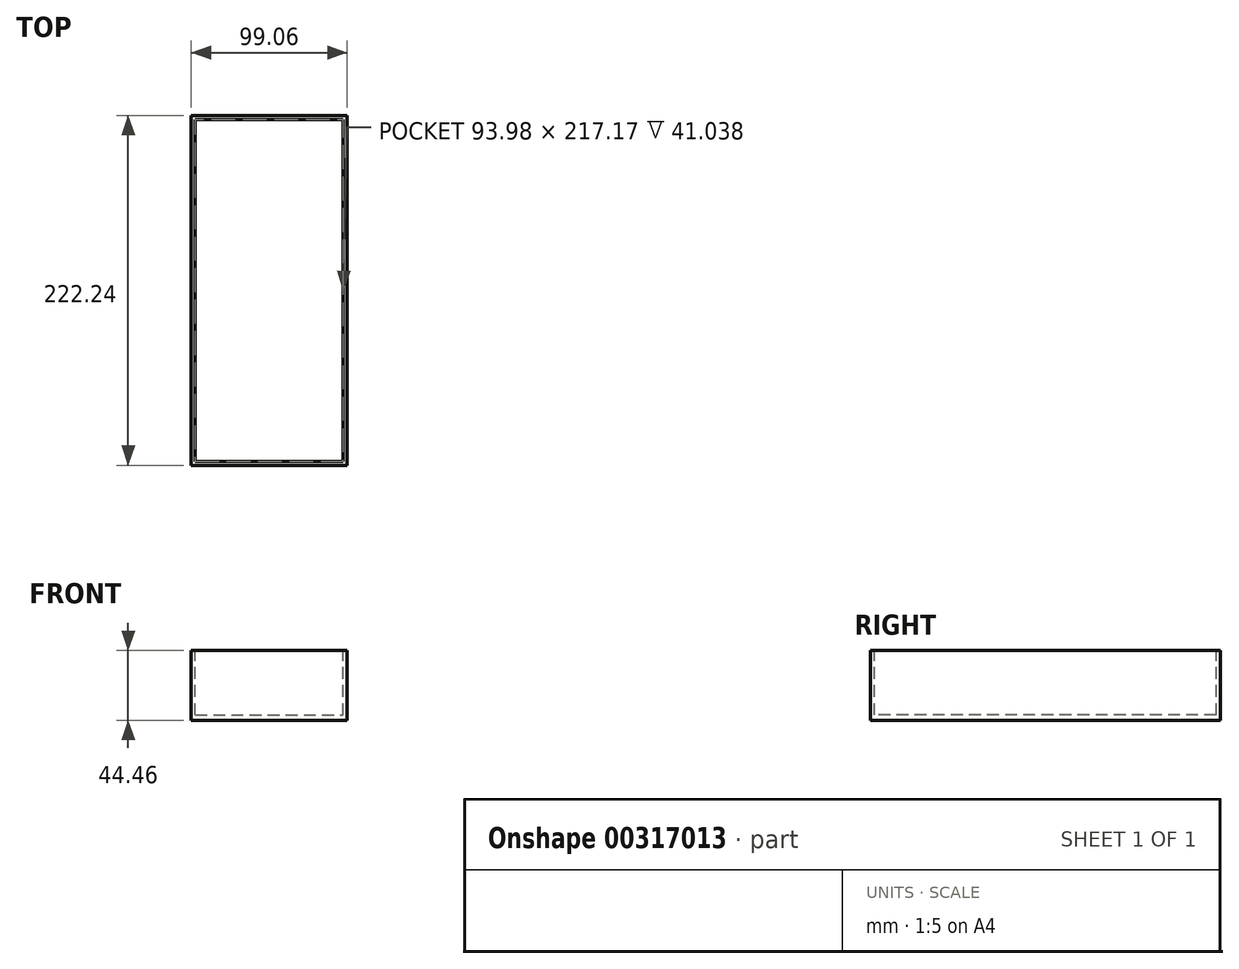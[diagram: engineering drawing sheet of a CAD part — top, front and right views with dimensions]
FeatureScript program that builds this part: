
annotation { "Feature Type Name" : "Feature", "Feature Type Description" : "" }
export const myFeature = defineFeature(function(context is Context, id is Id, definition is map)
    precondition{}
    {
        {
            var Q0;
            Q0=qCreatedBy(makeId("Top.planeOp"),FACE);
            var sketch = newSketch(context, id + "F0", { "sketchPlane" : qUnion([Q0])});
            skLineSegment(sketch, "E0.bottom", {"start": v(-46.99, 109.86) * mm, "end": v(47, 109.86) * mm});
            skLineSegment(sketch, "E0.top", {"start": v(-47, -109.86) * mm, "end": v(46.99, -109.86) * mm});
            skLineSegment(sketch, "E0.left", {"start": v(-46.99, 109.86) * mm, "end": v(-47, -109.86) * mm});
            skLineSegment(sketch, "E0.right", {"start": v(47, 109.85) * mm, "end": v(46.99, -109.86) * mm});
            skPoint(sketch, "E0.middle", {"position": v(0, 0) * mm});
            skSolve(sketch);
        }
        {
            var Q0;
            Q0 = qSketchRegion(id + "F0", true);
            extrude(context, id + "F1", {"entities" : qUnion([Q0]), "depth" : 20.95 * mm});
        }
        {
            var Q0;
            Q0=makeQuery(id+"F1.opExtrude","CAP_FACE",FACE,{"disambiguationData":[OSD([sQuery(id+"F0.wireOp",EDGE,"E0.bottom"),sQuery(id+"F0.wireOp",EDGE,"E0.top"),sQuery(id+"F0.wireOp",EDGE,"E0.left"),sQuery(id+"F0.wireOp",EDGE,"E0.right")])],"isStart":true});
            extrude(context, id + "F2", {"entities" : qUnion([Q0]), "operationType" : NewBodyOperationType.ADD, "depth" : 20.95 * mm});
        }
        {
            var Q0;
            {var subQ0=sQuery(id+"F0.wireOp",EDGE,"E0.left");Q0=makeQuery(id+"F2.boolean.opBoolean","MERGE",FACE,{"derivedFrom":[makeQuery(id+"F1.opExtrude","SWEPT_FACE",FACE,{"disambiguationData":[OSD([subQ0])]}),makeQuery(id+"F2.opExtrude","SWEPT_FACE",FACE,{"disambiguationData":[OSD([subQ0])]})]});}
            extrude(context, id + "F3", {"entities" : qUnion([Q0]), "operationType" : NewBodyOperationType.ADD, "depth" : 2.54 * mm});
        }
        {
            var Q0;
            {var subQ0=sQuery(id+"F0.wireOp",EDGE,"E0.right");Q0=makeQuery(id+"F2.boolean.opBoolean","MERGE",FACE,{"derivedFrom":[makeQuery(id+"F1.opExtrude","SWEPT_FACE",FACE,{"disambiguationData":[OSD([subQ0])]}),makeQuery(id+"F2.opExtrude","SWEPT_FACE",FACE,{"disambiguationData":[OSD([subQ0])]})]});}
            extrude(context, id + "F4", {"entities" : qUnion([Q0]), "operationType" : NewBodyOperationType.ADD, "depth" : 2.54 * mm});
        }
        {
            var Q0;
            {var subQ0=sQuery(id+"F0.wireOp",EDGE,"E0.right");var subQ1=sQuery(id+"F0.wireOp",EDGE,"E0.left");Q0=makeQuery(id+"F4.boolean.opBoolean","MERGE",FACE,{"derivedFrom":[makeQuery(id+"F3.boolean.opBoolean","MERGE",FACE,{"derivedFrom":[makeQuery(id+"F2.opExtrude","CAP_FACE",FACE,{"disambiguationData":[OSD([sQuery(id+"F0.wireOp",EDGE,"E0.bottom"),sQuery(id+"F0.wireOp",EDGE,"E0.top"),subQ1,subQ0])],"isStart":false}),makeQuery(id+"F3.opExtrude","SWEPT_FACE",FACE,{"disambiguationData":[OSD([subQ1]),TDD([makeQuery(id+"F2.opExtrude","CAP_EDGE",EDGE,{"disambiguationData":[OSD([subQ1])],"isStart":false})])]})]}),makeQuery(id+"F4.opExtrude","SWEPT_FACE",FACE,{"disambiguationData":[OSD([subQ0]),TDD([makeQuery(id+"F2.opExtrude","CAP_EDGE",EDGE,{"disambiguationData":[OSD([subQ0])],"isStart":false})])]})]});}
            extrude(context, id + "F5", {"entities" : qUnion([Q0]), "operationType" : NewBodyOperationType.ADD, "depth" : 2.54 * mm});
        }
        {
            var Q0;
            {var subQ0=sQuery(id+"F0.wireOp",EDGE,"E0.right");var subQ1=sQuery(id+"F0.wireOp",EDGE,"E0.left");var subQ2=sQuery(id+"F0.wireOp",EDGE,"E0.top");Q0=makeQuery(id+"F5z8EGmZ8wc2m9n_1.boolean.opBoolean","MERGE",FACE,{"derivedFrom":[makeQuery(id+"F5.boolean.opBoolean","MERGE",FACE,{"derivedFrom":[makeQuery(id+"F4.boolean.opBoolean","MERGE",FACE,{"derivedFrom":[makeQuery(id+"F3.boolean.opBoolean","MERGE",FACE,{"derivedFrom":[makeQuery(id+"F2.boolean.opBoolean","MERGE",FACE,{"derivedFrom":[makeQuery(id+"F1.opExtrude","SWEPT_FACE",FACE,{"disambiguationData":[OSD([subQ2])]}),makeQuery(id+"F2.opExtrude","SWEPT_FACE",FACE,{"disambiguationData":[OSD([subQ2])]})]}),makeQuery(id+"F3.opExtrude","SWEPT_FACE",FACE,{"disambiguationData":[OSD([subQ2,subQ1])]})]}),makeQuery(id+"F4.opExtrude","SWEPT_FACE",FACE,{"disambiguationData":[OSD([subQ2,subQ0])]})]}),makeQuery(id+"F5.opExtrude","SWEPT_FACE",FACE,{"disambiguationData":[OSD([subQ2,subQ1,subQ0])]})]}),makeQuery(id+"F5z8EGmZ8wc2m9n_1.opExtrude","SWEPT_FACE",FACE,{"disambiguationData":[OSD([subQ2,subQ1,subQ0])]})]});}
            var sketch = newSketch(context, id + "F6", { "sketchPlane" : qUnion([Q0])});
            skLineSegment(sketch, "E1", {"start": v(-49.53, -23.5) * mm, "end": v(-47, -23.5) * mm});
            skLineSegment(sketch, "E2", {"start": v(-47, -23.5) * mm, "end": v(-47, 23.5) * mm});
            skLineSegment(sketch, "E3", {"start": v(-49.53, 23.5) * mm, "end": v(-49.53, 20.96) * mm});
            skLineSegment(sketch, "E4", {"start": v(-49.53, 20.96) * mm, "end": v(49.53, 20.96) * mm});
            skLineSegment(sketch, "E5", {"start": v(-49.53, -20.08) * mm, "end": v(49.53, -20.08) * mm});
            skLineSegment(sketch, "E6", {"start": v(49.53, -23.5) * mm, "end": v(46.99, -23.5) * mm});
            skLineSegment(sketch, "E7", {"start": v(46.99, -23.5) * mm, "end": v(46.99, 23.5) * mm});
            skSolve(sketch);
        }
        {
            var Q0;
            {var subQ0=sQuery(id+"F0.wireOp",EDGE,"E0.right");var subQ1=sQuery(id+"F0.wireOp",EDGE,"E0.left");var subQ2=sQuery(id+"F0.wireOp",EDGE,"E0.bottom");Q0=makeQuery(id+"F5z8EGmZ8wc2m9n_1.boolean.opBoolean","MERGE",FACE,{"derivedFrom":[makeQuery(id+"F5.boolean.opBoolean","MERGE",FACE,{"derivedFrom":[makeQuery(id+"F4.boolean.opBoolean","MERGE",FACE,{"derivedFrom":[makeQuery(id+"F3.boolean.opBoolean","MERGE",FACE,{"derivedFrom":[makeQuery(id+"F2.boolean.opBoolean","MERGE",FACE,{"derivedFrom":[makeQuery(id+"F1.opExtrude","SWEPT_FACE",FACE,{"disambiguationData":[OSD([subQ2])]}),makeQuery(id+"F2.opExtrude","SWEPT_FACE",FACE,{"disambiguationData":[OSD([subQ2])]})]}),makeQuery(id+"F3.opExtrude","SWEPT_FACE",FACE,{"disambiguationData":[OSD([subQ2,subQ1])]})]}),makeQuery(id+"F4.opExtrude","SWEPT_FACE",FACE,{"disambiguationData":[OSD([subQ2,subQ0])]})]}),makeQuery(id+"F5.opExtrude","SWEPT_FACE",FACE,{"disambiguationData":[OSD([subQ2,subQ1,subQ0])]})]}),makeQuery(id+"F5z8EGmZ8wc2m9n_1.opExtrude","SWEPT_FACE",FACE,{"disambiguationData":[OSD([subQ2,subQ1,subQ0])]})]});}
            extrude(context, id + "F7", {"entities" : qUnion([Q0]), "operationType" : NewBodyOperationType.ADD, "depth" : 2.54 * mm});
        }
        {
            var Q0;
            {var subQ0=sQuery(id+"F6.wireOp",EDGE,"E5");var subQ1=sQuery(id+"F6.wireOp",EDGE,"E2");var subQ2=makeQuery(id+"F6.imprint","INTERSECT",VERTEX,{"derivedFrom":[subQ1,subQ0]});Q0=makeQuery(id+"F6.imprint","IMPRINT",FACE,{"disambiguationData":[TD([[makeQuery(id+"F6.imprint","IMPRINT",EDGE,{"disambiguationData":[TD([[subQ2,-1.0]])],"derivedFrom":subQ1}),-1.0]])]});}
            extrude(context, id + "F8", {"entities" : qUnion([Q0]), "operationType" : NewBodyOperationType.REMOVE, "oppositeDirection" : true, "depth" : 219.71 * mm});
        }
        {
            var Q0;
            Q0 = qSketchRegion(id + "F6", true);
            extrude(context, id + "F9", {"entities" : qUnion([Q0]), "operationType" : NewBodyOperationType.ADD, "oppositeDirection" : true, "depth" : 2.54 * mm});
        }
    });
